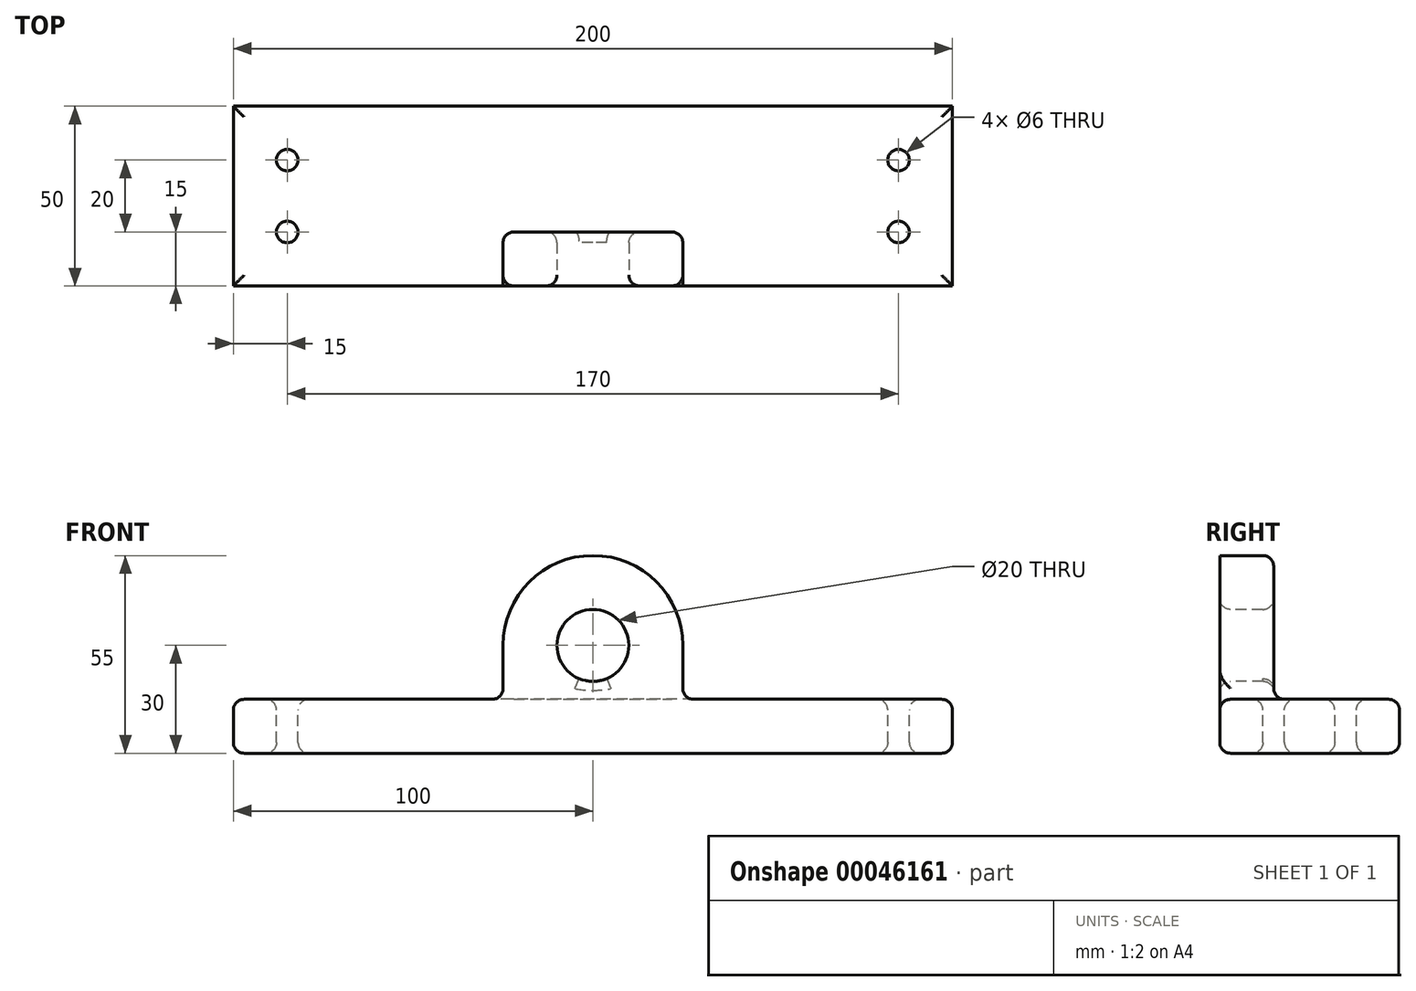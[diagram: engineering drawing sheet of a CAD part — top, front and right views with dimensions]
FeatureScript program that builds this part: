
annotation { "Feature Type Name" : "Feature", "Feature Type Description" : "" }
export const myFeature = defineFeature(function(context is Context, id is Id, definition is map)
    precondition{}
    {
        {
            var Q0;
            Q0=qCreatedBy(makeId("Top.planeOp"),FACE);
            var sketch = newSketch(context, id + "F0", { "sketchPlane" : qUnion([Q0])});
            skLineSegment(sketch, "E0.rect.bottom", {"start": v(100, 25) * mm, "end": v(-100, 25) * mm});
            skLineSegment(sketch, "E0.rect.top", {"start": v(100, -25) * mm, "end": v(-100, -25) * mm});
            skLineSegment(sketch, "E0.rect.left", {"start": v(100, 25) * mm, "end": v(100, -25) * mm});
            skLineSegment(sketch, "E0.rect.right", {"start": v(-100, 25) * mm, "end": v(-100, -25) * mm});
            skPoint(sketch, "E0.rect.middle", {"position": v(0, 0) * mm});
            skSolve(sketch);
        }
        {
            var Q0;
            Q0=makeQuery(id+"F0.imprint","IMPRINT",FACE,{"disambiguationData":[TD([[makeQuery(id+"F0.imprint","IMPRINT",EDGE,{"derivedFrom":sQuery(id+"F0.wireOp",EDGE,"E0.rect.bottom")}),1.0]])]});
            extrude(context, id + "F1", {"entities" : qUnion([Q0]), "depth" : 15 * mm});
        }
        {
            var Q0;
            Q0=makeQuery(id+"F1.opExtrude","SWEPT_FACE",FACE,{"disambiguationData":[OSD([sQuery(id+"F0.wireOp",EDGE,"E0.rect.top")])]});
            var sketch = newSketch(context, id + "F2", { "sketchPlane" : qUnion([Q0])});
            skLineSegment(sketch, "E1", {"start": v(0, 0) * mm, "end": v(0, 30) * mm, "construction": true});
            skPoint(sketch, "E1.endSnap0", {"position": v(0, 15) * mm});
            skCircle(sketch, "E2", {"center": v(0, 30) * mm, "radius": 25 * mm});
            skLineSegment(sketch, "E3.bottom", {"start": v(-25, 30) * mm, "end": v(25, 30) * mm});
            skLineSegment(sketch, "E3.top", {"start": v(-25, 0) * mm, "end": v(25, 0) * mm});
            skLineSegment(sketch, "E3.left", {"start": v(-25, 30) * mm, "end": v(-25, 0) * mm});
            skLineSegment(sketch, "E3.right", {"start": v(25, 30) * mm, "end": v(25, 0) * mm});
            skCircle(sketch, "E4", {"center": v(0, 30) * mm, "radius": 10 * mm});
            skSolve(sketch);
        }
        {
            var Q0;
            {var subQ0=sQuery(id+"F2.wireOp",EDGE,"E3.bottom");var subQ1=sQuery(id+"F2.wireOp",EDGE,"E4");var subQ5=makeQuery(id+"F2.imprint","INTERSECT",VERTEX,{"disambiguationData":[OD(0.0)],"derivedFrom":[subQ0,subQ1]});Q0=makeQuery(id+"F2.imprint","IMPRINT",FACE,{"disambiguationData":[TD([[makeQuery(id+"F2.imprint","IMPRINT",EDGE,{"disambiguationData":[TD([[subQ5,1.0]])],"derivedFrom":subQ1}),-1.0]])]});}
            var Q1;
            {var subQ4=sQuery(id+"F2.wireOp",EDGE,"E4");var subQ5=sQuery(id+"F2.wireOp",EDGE,"E3.bottom");var subQ7=makeQuery(id+"F2.imprint","INTERSECT",VERTEX,{"disambiguationData":[OD(0.0)],"derivedFrom":[subQ5,subQ4]});Q1=makeQuery(id+"F2.imprint","IMPRINT",FACE,{"disambiguationData":[TD([[makeQuery(id+"F2.imprint","IMPRINT",EDGE,{"disambiguationData":[TD([[subQ7,-1.0]])],"derivedFrom":subQ4}),-1.0]])]});}
            var Q2;
            {var subQ0=sQuery(id+"F2.wireOp",EDGE,"E3.left");var subQ1=makeQuery(id+"F1.opExtrude","CAP_EDGE",EDGE,{"disambiguationData":[OSD([sQuery(id+"F0.wireOp",EDGE,"E0.rect.top")])],"isStart":false});var subQ2=makeQuery(id+"F2.imprint","INTERSECT",VERTEX,{"derivedFrom":[subQ1,subQ0]});Q2=makeQuery(id+"F2.imprint","IMPRINT",FACE,{"disambiguationData":[TD([[makeQuery(id+"F2.imprint","IMPRINT",EDGE,{"disambiguationData":[TD([[subQ2,1.0]])],"derivedFrom":subQ1}),-1.0]])]});}
            var Q3;
            {var subQ0=makeQuery(id+"F1.opExtrude","CAP_EDGE",EDGE,{"disambiguationData":[OSD([sQuery(id+"F0.wireOp",EDGE,"E0.rect.top")])],"isStart":false});var subQ3=sQuery(id+"F2.wireOp",EDGE,"E3.right");var subQ4=makeQuery(id+"F2.imprint","INTERSECT",VERTEX,{"derivedFrom":[subQ0,subQ3]});Q3=makeQuery(id+"F2.imprint","IMPRINT",FACE,{"disambiguationData":[TD([[makeQuery(id+"F2.imprint","IMPRINT",EDGE,{"disambiguationData":[TD([[subQ4,-1.0]])],"derivedFrom":subQ0}),-1.0]])]});}
            var Q4;
            {var subQ7=sQuery(id+"F2.wireOp",EDGE,"E3.top");Q4=makeQuery(id+"F2.imprint","IMPRINT",FACE,{"disambiguationData":[TD([[makeQuery(id+"F2.imprint","IMPRINT",EDGE,{"derivedFrom":subQ7}),-1.0]])]});}
            var Q5;
            Q5=makeQuery(id+"F1.opExtrude","SWEPT_FACE",FACE,{"disambiguationData":[OSD([sQuery(id+"F0.wireOp",EDGE,"E0.rect.bottom")])]});
            extrude(context, id + "F3", {"entities" : qUnion([Q0, Q1, Q2, Q3, Q4]), "operationType" : NewBodyOperationType.ADD, "oppositeDirection" : true, "endBoundEntityFace" : qUnion([Q5]), "depth" : 15 * mm});
        }
        {
            var Q0;
            Q0=makeQuery(id+"F1.opExtrude","CAP_FACE",FACE,{"disambiguationData":[OSD([sQuery(id+"F0.wireOp",EDGE,"E0.rect.bottom"),sQuery(id+"F0.wireOp",EDGE,"E0.rect.top"),sQuery(id+"F0.wireOp",EDGE,"E0.rect.left"),sQuery(id+"F0.wireOp",EDGE,"E0.rect.right")])],"isStart":false});
            var sketch = newSketch(context, id + "F4", { "sketchPlane" : qUnion([Q0])});
            skLineSegment(sketch, "E5.rect.bottom", {"start": v(85, -10) * mm, "end": v(-85, -10) * mm, "construction": true});
            skLineSegment(sketch, "E5.rect.top", {"start": v(85, 10) * mm, "end": v(-85, 10) * mm, "construction": true});
            skLineSegment(sketch, "E5.rect.left", {"start": v(85, -10) * mm, "end": v(85, 10) * mm, "construction": true});
            skLineSegment(sketch, "E5.rect.right", {"start": v(-85, -10) * mm, "end": v(-85, 10) * mm, "construction": true});
            skPoint(sketch, "E5.rect.middle", {"position": v(0, 0) * mm});
            skCircle(sketch, "E6", {"center": v(-85, 10) * mm, "radius": 3 * mm});
            skCircle(sketch, "E7", {"center": v(-85, -10) * mm, "radius": 3 * mm});
            skCircle(sketch, "E8", {"center": v(85, 10) * mm, "radius": 3 * mm});
            skCircle(sketch, "E9", {"center": v(85, -10) * mm, "radius": 3 * mm});
            skSolve(sketch);
        }
        {
            var Q0;
            Q0=makeQuery(id+"F4.imprint","IMPRINT",FACE,{"disambiguationData":[TD([[makeQuery(id+"F4.imprint","IMPRINT",EDGE,{"derivedFrom":sQuery(id+"F4.wireOp",EDGE,"E7")}),1.0]])]});
            var Q1;
            Q1=makeQuery(id+"F4.imprint","IMPRINT",FACE,{"disambiguationData":[TD([[makeQuery(id+"F4.imprint","IMPRINT",EDGE,{"derivedFrom":sQuery(id+"F4.wireOp",EDGE,"E8")}),1.0]])]});
            var Q2;
            Q2=makeQuery(id+"F4.imprint","IMPRINT",FACE,{"disambiguationData":[TD([[makeQuery(id+"F4.imprint","IMPRINT",EDGE,{"derivedFrom":sQuery(id+"F4.wireOp",EDGE,"E9")}),1.0]])]});
            var Q3;
            Q3=makeQuery(id+"F4.imprint","IMPRINT",FACE,{"disambiguationData":[TD([[makeQuery(id+"F4.imprint","IMPRINT",EDGE,{"derivedFrom":sQuery(id+"F4.wireOp",EDGE,"E6")}),1.0]])]});
            extrude(context, id + "F5", {"entities" : qUnion([Q0, Q1, Q2, Q3]), "operationType" : NewBodyOperationType.REMOVE, "endBound" : BoundingType.UP_TO_NEXT, "oppositeDirection" : true, "depth" : 25 * mm});
        }
        {
            var Q0;
            Q0=makeQuery(id+"F1.opExtrude","CAP_FACE",FACE,{"disambiguationData":[OSD([sQuery(id+"F0.wireOp",EDGE,"E0.rect.bottom"),sQuery(id+"F0.wireOp",EDGE,"E0.rect.top"),sQuery(id+"F0.wireOp",EDGE,"E0.rect.left"),sQuery(id+"F0.wireOp",EDGE,"E0.rect.right")])],"isStart":false});
            var Q1;
            Q1=makeQuery(id+"F1.opExtrude","CAP_FACE",FACE,{"disambiguationData":[OSD([sQuery(id+"F0.wireOp",EDGE,"E0.rect.bottom"),sQuery(id+"F0.wireOp",EDGE,"E0.rect.top"),sQuery(id+"F0.wireOp",EDGE,"E0.rect.left"),sQuery(id+"F0.wireOp",EDGE,"E0.rect.right")])],"isStart":true});
            var Q2;
            Q2=makeQuery(id+"F3.opExtrude","CAP_EDGE",EDGE,{"disambiguationData":[OSD([sQuery(id+"F2.wireOp",EDGE,"E3.right")])],"isStart":false});
            var Q3;
            Q3=makeQuery(id+"F3.opExtrude","CAP_EDGE",EDGE,{"disambiguationData":[OSD([sQuery(id+"F2.wireOp",EDGE,"E4")])],"isStart":true});
            fillet(context, id + "F6", {"entities" : qUnion([Q0, Q1, Q2, Q3]), "radius" : 3 * mm, "tangentPropagation" : true, "allowEdgeOverflow" : false});
        }
        {
            var Q0;
            Q0=makeQuery(id+"F3.opExtrude","CAP_EDGE",EDGE,{"disambiguationData":[OSD([sQuery(id+"F2.wireOp",EDGE,"E4")])],"isStart":false});
            fillet(context, id + "F7", {"entities" : qUnion([Q0]), "radius" : 3 * mm, "tangentPropagation" : true, "allowEdgeOverflow" : false});
        }
    });
